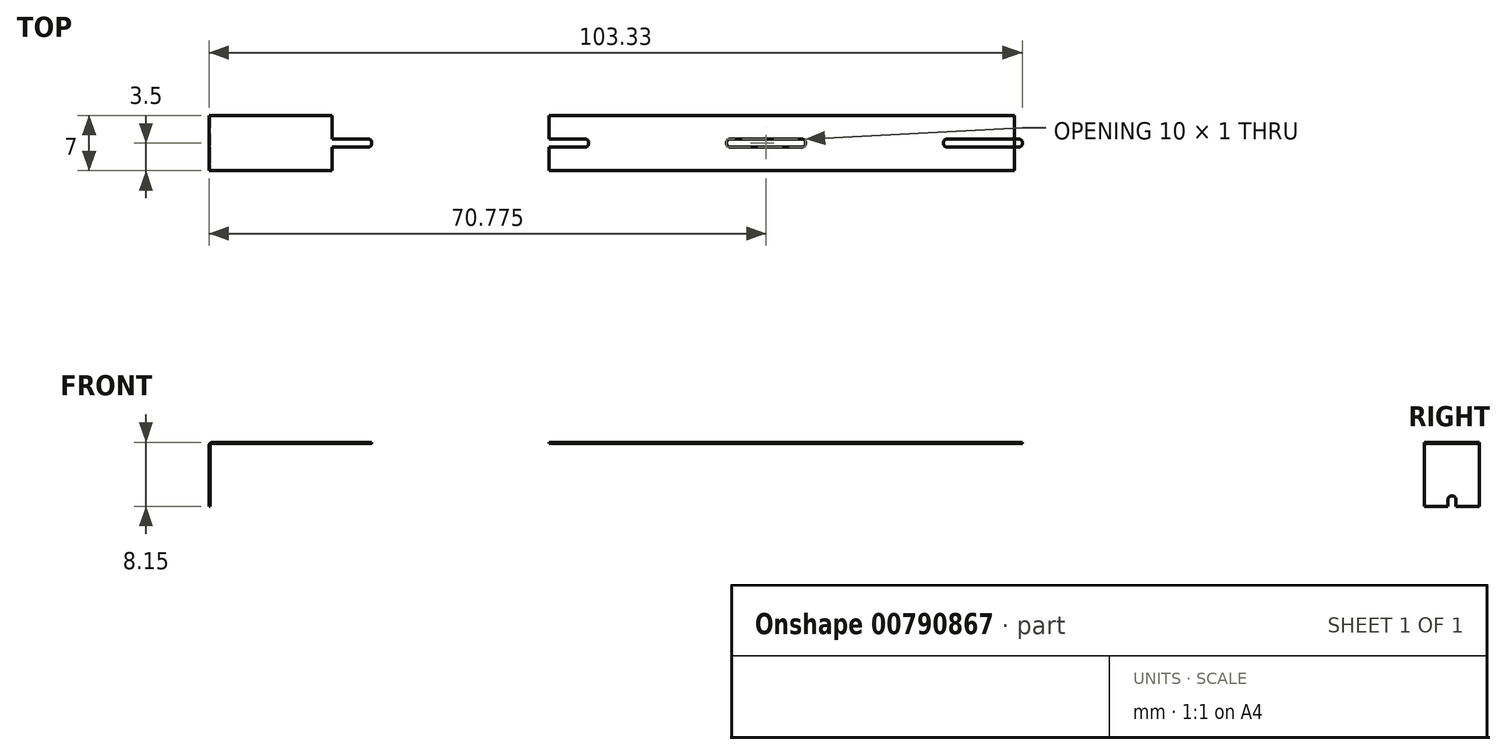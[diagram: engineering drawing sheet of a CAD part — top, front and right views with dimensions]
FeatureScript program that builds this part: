
annotation { "Feature Type Name" : "Feature", "Feature Type Description" : "" }
export const myFeature = defineFeature(function(context is Context, id is Id, definition is map)
    precondition{}
    {
        {
            var Q0;
            Q0=qCreatedBy(makeId("Top.planeOp"),FACE);
            var sketch = newSketch(context, id + "F0", { "sketchPlane" : qUnion([Q0])});
            skPoint(sketch, "E0.middle", {"position": v(0, 0) * mm});
            skLineSegment(sketch, "E1.bottom", {"start": v(-9.18, -0.5) * mm, "end": v(-13.77, -0.5) * mm});
            skLineSegment(sketch, "E1.top", {"start": v(-9.18, 0.5) * mm, "end": v(-13.77, 0.5) * mm});
            skLineSegment(sketch, "E1.left", {"start": v(-8.78, -0.1) * mm, "end": v(-8.78, 0.1) * mm});
            skLineSegment(sketch, "E1.right", {"start": v(-18.78, -0.1) * mm, "end": v(-18.78, 0.1) * mm});
            skPoint(sketch, "E1.middle", {"position": v(-13.78, 0) * mm});
            skPoint(sketch, "E2.visualSharp", {"position": v(-8.78, 0.5) * mm});
            skArc(sketch, "E2.filletArc", {"start": v(-8.78, 0.1) * mm, "mid": v(-8.9, 0.38) * mm, "end": v(-9.18, 0.5) * mm});
            skPoint(sketch, "E3.visualSharp", {"position": v(-8.78, -0.5) * mm});
            skArc(sketch, "E3.filletArc", {"start": v(-9.18, -0.5) * mm, "mid": v(-8.9, -0.38) * mm, "end": v(-8.78, -0.1) * mm});
            skPoint(sketch, "E4.visualSharp", {"position": v(-18.78, 0.5) * mm});
            skArc(sketch, "E4.filletArc", {"start": v(-18.38, 0.5) * mm, "mid": v(-18.66, 0.38) * mm, "end": v(-18.77, 0.1) * mm});
            skPoint(sketch, "E5.visualSharp", {"position": v(-18.78, -0.5) * mm});
            skArc(sketch, "E5.filletArc", {"start": v(-18.77, -0.1) * mm, "mid": v(-18.66, -0.38) * mm, "end": v(-18.38, -0.5) * mm});
            skLineSegment(sketch, "E6", {"start": v(0, 3.5) * mm, "end": v(-13.78, 3.5) * mm});
            skPoint(sketch, "E6.endSnap0", {"position": v(-13.77, 0.5) * mm});
            skLineSegment(sketch, "E7", {"start": v(-13.78, 3.5) * mm, "end": v(-13.78, 0.5) * mm});
            skLineSegment(sketch, "E8.MirrorCS", {"start": v(0, -3.5) * mm, "end": v(-13.78, -3.5) * mm});
            skLineSegment(sketch, "E9.MirrorCS", {"start": v(-13.78, -3.5) * mm, "end": v(-13.78, -0.5) * mm});
            skLineSegment(sketch, "E10.MirrorCS", {"start": v(0, 3.5) * mm, "end": v(13.78, 3.5) * mm});
            skLineSegment(sketch, "E11.MirrorCS", {"start": v(0, -3.5) * mm, "end": v(13.78, -3.5) * mm});
            skLineSegment(sketch, "E12.MirrorCS", {"start": v(8.78, -0.1) * mm, "end": v(8.78, 0.1) * mm});
            skArc(sketch, "E13.MirrorCS", {"start": v(8.78, 0.1) * mm, "mid": v(8.9, 0.38) * mm, "end": v(9.18, 0.5) * mm});
            skArc(sketch, "E14.MirrorCS", {"start": v(18.77, -0.1) * mm, "mid": v(18.66, -0.38) * mm, "end": v(18.38, -0.5) * mm});
            skLineSegment(sketch, "E15.MirrorCS", {"start": v(18.78, -0.1) * mm, "end": v(18.78, 0.1) * mm});
            skArc(sketch, "E16.MirrorCS", {"start": v(18.38, 0.5) * mm, "mid": v(18.66, 0.38) * mm, "end": v(18.77, 0.1) * mm});
            skArc(sketch, "E17.MirrorCS", {"start": v(9.18, -0.5) * mm, "mid": v(8.9, -0.38) * mm, "end": v(8.78, -0.1) * mm});
            skPoint(sketch, "E18.MirrorP", {"position": v(18.78, 0.5) * mm});
            skLineSegment(sketch, "E19.MirrorCS", {"start": v(9.18, 0.5) * mm, "end": v(18.38, 0.5) * mm});
            skLineSegment(sketch, "E20.MirrorCS", {"start": v(9.18, -0.5) * mm, "end": v(18.38, -0.5) * mm});
            skPoint(sketch, "E21.MirrorP", {"position": v(13.77, 0.5) * mm});
            skPoint(sketch, "E22.MirrorP", {"position": v(8.78, 0.5) * mm});
            skPoint(sketch, "E23.MirrorP", {"position": v(18.78, -0.5) * mm});
            skPoint(sketch, "E24.MirrorP", {"position": v(8.78, -0.5) * mm});
            skPoint(sketch, "E25.MirrorP", {"position": v(13.78, 0) * mm});
            skLineSegment(sketch, "E26.MirrorCS", {"start": v(13.78, 3.5) * mm, "end": v(13.78, 0.5) * mm});
            skLineSegment(sketch, "E27.MirrorCS", {"start": v(13.78, -3.5) * mm, "end": v(13.78, -0.5) * mm});
            skPoint(sketch, "E28.1.0.0", {"position": v(36.33, 0.5) * mm});
            skLineSegment(sketch, "E28.1.0.1", {"start": v(27.55, 3.5) * mm, "end": v(41.33, 3.5) * mm});
            skLineSegment(sketch, "E28.1.0.2", {"start": v(36.73, -0.5) * mm, "end": v(45.93, -0.5) * mm});
            skPoint(sketch, "E28.1.0.3", {"position": v(27.55, 0) * mm});
            skLineSegment(sketch, "E28.1.0.4", {"start": v(27.55, -3.5) * mm, "end": v(41.33, -3.5) * mm});
            skPoint(sketch, "E28.1.0.5", {"position": v(41.33, 0.5) * mm});
            skPoint(sketch, "E28.1.0.6", {"position": v(41.33, 0) * mm});
            skPoint(sketch, "E28.1.0.7", {"position": v(46.33, -0.5) * mm});
            skPoint(sketch, "E28.1.0.8", {"position": v(36.33, -0.5) * mm});
            skLineSegment(sketch, "E28.1.0.9", {"start": v(27.55, -3.5) * mm, "end": v(13.78, -3.5) * mm});
            skLineSegment(sketch, "E28.1.0.10", {"start": v(36.73, 0.5) * mm, "end": v(45.93, 0.5) * mm});
            skLineSegment(sketch, "E28.1.0.11", {"start": v(27.55, 3.5) * mm, "end": v(13.78, 3.5) * mm});
            skLineSegment(sketch, "E28.1.0.12", {"start": v(41.33, 3.5) * mm, "end": v(41.33, 0.5) * mm});
            skLineSegment(sketch, "E28.1.0.13", {"start": v(41.33, -3.5) * mm, "end": v(41.33, -0.5) * mm});
            skPoint(sketch, "E28.1.0.14", {"position": v(46.33, 0.5) * mm});
            skArc(sketch, "E28.1.0.15", {"start": v(45.93, 0.5) * mm, "mid": v(46.2, 0.38) * mm, "end": v(46.32, 0.1) * mm});
            skArc(sketch, "E28.1.0.16", {"start": v(36.73, -0.5) * mm, "mid": v(36.44, -0.38) * mm, "end": v(36.33, -0.1) * mm});
            skArc(sketch, "E28.1.0.17", {"start": v(46.33, -0.1) * mm, "mid": v(46.2, -0.38) * mm, "end": v(45.93, -0.5) * mm});
            skArc(sketch, "E28.1.0.18", {"start": v(36.33, 0.1) * mm, "mid": v(36.44, 0.38) * mm, "end": v(36.73, 0.5) * mm});
            skLineSegment(sketch, "E28.1.0.19", {"start": v(36.32, -0.1) * mm, "end": v(36.32, 0.1) * mm});
            skLineSegment(sketch, "E28.1.0.20", {"start": v(46.33, -0.1) * mm, "end": v(46.33, 0.1) * mm});
            skPoint(sketch, "E28.2.0.0", {"position": v(63.88, 0.5) * mm});
            skLineSegment(sketch, "E28.2.0.1", {"start": v(55.1, 3.5) * mm, "end": v(68.88, 3.5) * mm});
            skLineSegment(sketch, "E28.2.0.2", {"start": v(64.28, -0.5) * mm, "end": v(73.48, -0.5) * mm});
            skPoint(sketch, "E28.2.0.3", {"position": v(55.1, 0) * mm});
            skLineSegment(sketch, "E28.2.0.4", {"start": v(55.1, -3.5) * mm, "end": v(68.88, -3.5) * mm});
            skPoint(sketch, "E28.2.0.5", {"position": v(68.88, 0.5) * mm});
            skPoint(sketch, "E28.2.0.6", {"position": v(68.88, 0) * mm});
            skPoint(sketch, "E28.2.0.7", {"position": v(73.88, -0.5) * mm});
            skPoint(sketch, "E28.2.0.8", {"position": v(63.88, -0.5) * mm});
            skLineSegment(sketch, "E28.2.0.9", {"start": v(55.1, -3.5) * mm, "end": v(41.33, -3.5) * mm});
            skLineSegment(sketch, "E28.2.0.10", {"start": v(64.28, 0.5) * mm, "end": v(73.48, 0.5) * mm});
            skLineSegment(sketch, "E28.2.0.11", {"start": v(55.1, 3.5) * mm, "end": v(41.33, 3.5) * mm});
            skLineSegment(sketch, "E28.2.0.12", {"start": v(68.88, 3.5) * mm, "end": v(68.88, 0.5) * mm});
            skLineSegment(sketch, "E28.2.0.13", {"start": v(68.88, -3.5) * mm, "end": v(68.88, -0.5) * mm});
            skPoint(sketch, "E28.2.0.14", {"position": v(73.88, 0.5) * mm});
            skArc(sketch, "E28.2.0.15", {"start": v(73.48, 0.5) * mm, "mid": v(73.76, 0.38) * mm, "end": v(73.88, 0.1) * mm});
            skArc(sketch, "E28.2.0.16", {"start": v(64.28, -0.5) * mm, "mid": v(64, -0.38) * mm, "end": v(63.88, -0.1) * mm});
            skArc(sketch, "E28.2.0.17", {"start": v(73.88, -0.1) * mm, "mid": v(73.76, -0.38) * mm, "end": v(73.48, -0.5) * mm});
            skArc(sketch, "E28.2.0.18", {"start": v(63.88, 0.1) * mm, "mid": v(64, 0.38) * mm, "end": v(64.28, 0.5) * mm});
            skLineSegment(sketch, "E28.2.0.19", {"start": v(63.88, -0.1) * mm, "end": v(63.88, 0.1) * mm});
            skLineSegment(sketch, "E28.2.0.20", {"start": v(73.88, -0.1) * mm, "end": v(73.88, 0.1) * mm});
            skPoint(sketch, "E28.3.0.0", {"position": v(91.43, 0.5) * mm});
            skLineSegment(sketch, "E28.3.0.1", {"start": v(82.65, 3.5) * mm, "end": v(96.43, 3.5) * mm});
            skLineSegment(sketch, "E28.3.0.2", {"start": v(91.83, -0.5) * mm, "end": v(101.03, -0.5) * mm});
            skPoint(sketch, "E28.3.0.3", {"position": v(82.65, 0) * mm});
            skLineSegment(sketch, "E28.3.0.4", {"start": v(82.65, -3.5) * mm, "end": v(96.43, -3.5) * mm});
            skPoint(sketch, "E28.3.0.5", {"position": v(96.43, 0.5) * mm});
            skPoint(sketch, "E28.3.0.6", {"position": v(96.42, 0) * mm});
            skPoint(sketch, "E28.3.0.7", {"position": v(101.42, -0.5) * mm});
            skPoint(sketch, "E28.3.0.8", {"position": v(91.43, -0.5) * mm});
            skLineSegment(sketch, "E28.3.0.9", {"start": v(82.65, -3.5) * mm, "end": v(68.88, -3.5) * mm});
            skLineSegment(sketch, "E28.3.0.10", {"start": v(91.83, 0.5) * mm, "end": v(101.03, 0.5) * mm});
            skLineSegment(sketch, "E28.3.0.11", {"start": v(82.65, 3.5) * mm, "end": v(68.88, 3.5) * mm});
            skLineSegment(sketch, "E28.3.0.12", {"start": v(96.43, 3.5) * mm, "end": v(96.43, 0.5) * mm});
            skLineSegment(sketch, "E28.3.0.13", {"start": v(96.43, -3.5) * mm, "end": v(96.43, -0.5) * mm});
            skPoint(sketch, "E28.3.0.14", {"position": v(101.42, 0.5) * mm});
            skArc(sketch, "E28.3.0.15", {"start": v(101.03, 0.5) * mm, "mid": v(101.3, 0.38) * mm, "end": v(101.42, 0.1) * mm});
            skArc(sketch, "E28.3.0.16", {"start": v(91.83, -0.5) * mm, "mid": v(91.54, -0.38) * mm, "end": v(91.43, -0.1) * mm});
            skArc(sketch, "E28.3.0.17", {"start": v(101.42, -0.1) * mm, "mid": v(101.3, -0.38) * mm, "end": v(101.03, -0.5) * mm});
            skArc(sketch, "E28.3.0.18", {"start": v(91.43, 0.1) * mm, "mid": v(91.54, 0.38) * mm, "end": v(91.83, 0.5) * mm});
            skLineSegment(sketch, "E28.3.0.19", {"start": v(91.43, -0.1) * mm, "end": v(91.43, 0.1) * mm});
            skLineSegment(sketch, "E28.3.0.20", {"start": v(101.42, -0.1) * mm, "end": v(101.42, 0.1) * mm});
            skLineSegment(sketch, "E28.direction1", {"start": v(-13.78, -3.5) * mm, "end": v(13.78, -3.5) * mm, "construction": true});
            skLineSegment(sketch, "E29", {"start": v(0, 3.5) * mm, "end": v(0, -3.5) * mm});
            skLineSegment(sketch, "E30.bottom", {"start": v(96.43, -3.5) * mm, "end": v(100.42, -3.5) * mm});
            skLineSegment(sketch, "E30.top", {"start": v(96.43, 3.5) * mm, "end": v(100.42, 3.5) * mm});
            skLineSegment(sketch, "E30.left", {"start": v(96.43, -3.5) * mm, "end": v(96.43, 3.5) * mm});
            skLineSegment(sketch, "E31", {"start": v(100.42, -3.5) * mm, "end": v(100.42, 3.5) * mm});
            skSolve(sketch);
        }
        {
            var Q0;
            {var subQ8=sQuery(id+"F0.wireOp",EDGE,"E28.3.0.12");Q0=makeQuery(id+"F0.imprint","IMPRINT",FACE,{"disambiguationData":[TD([[makeQuery(id+"F0.imprint","IMPRINT",EDGE,{"derivedFrom":subQ8}),1.0]])]});}
            var Q1;
            {var subQ3=sQuery(id+"F0.wireOp",EDGE,"E14.MirrorCS");Q1=makeQuery(id+"F0.imprint","IMPRINT",FACE,{"disambiguationData":[TD([[makeQuery(id+"F0.imprint","IMPRINT",EDGE,{"derivedFrom":subQ3}),1.0]])]});}
            var Q2;
            {var subQ8=sQuery(id+"F0.wireOp",EDGE,"E28.1.0.12");Q2=makeQuery(id+"F0.imprint","IMPRINT",FACE,{"disambiguationData":[TD([[makeQuery(id+"F0.imprint","IMPRINT",EDGE,{"derivedFrom":subQ8}),1.0]])]});}
            var Q3;
            {var subQ8=sQuery(id+"F0.wireOp",EDGE,"E28.2.0.12");Q3=makeQuery(id+"F0.imprint","IMPRINT",FACE,{"disambiguationData":[TD([[makeQuery(id+"F0.imprint","IMPRINT",EDGE,{"derivedFrom":subQ8}),1.0]])]});}
            var Q4;
            Q4=makeQuery(id+"F0.imprint","IMPRINT",FACE,{"disambiguationData":[TD([[makeQuery(id+"F0.imprint","IMPRINT",EDGE,{"derivedFrom":sQuery(id+"F0.wireOp",EDGE,"E10.MirrorCS")}),-1.0]])]});
            var Q5;
            {var subQ5=sQuery(id+"F0.wireOp",EDGE,"E30.top");Q5=makeQuery(id+"F0.imprint","IMPRINT",FACE,{"disambiguationData":[TD([[makeQuery(id+"F0.imprint","IMPRINT",EDGE,{"derivedFrom":subQ5}),-1.0]])]});}
            var Q6;
            {var subQ5=sQuery(id+"F0.wireOp",EDGE,"E30.bottom");Q6=makeQuery(id+"F0.imprint","IMPRINT",FACE,{"disambiguationData":[TD([[makeQuery(id+"F0.imprint","IMPRINT",EDGE,{"derivedFrom":subQ5}),1.0]])]});}
            var Q7;
            {var subQ11=sQuery(id+"F0.wireOp",EDGE,"E28.3.0.15");Q7=makeQuery(id+"F0.imprint","IMPRINT",FACE,{"disambiguationData":[TD([[makeQuery(id+"F0.imprint","IMPRINT",EDGE,{"derivedFrom":subQ11}),1.0]])]});}
            extrude(context, id + "F1", {"entities" : qUnion([Q0, Q1, Q2, Q3, Q4, Q5, Q6, Q7]), "depth" : 0.15 * mm, "offsetDistance" : 25 * mm});
        }
        {
            var Q0;
            Q0=makeQuery(id+"F1.opExtrude","SWEPT_FACE",FACE,{"disambiguationData":[OSD([sQuery(id+"F0.wireOp",EDGE,"E29")])]});
            extrude(context, id + "F2", {"entities" : qUnion([Q0]), "operationType" : NewBodyOperationType.ADD, "depth" : 1.9 * mm, "offsetDistance" : 25 * mm});
        }
        {
            var Q0;
            {var subQ0=sQuery(id+"F0.wireOp",EDGE,"E29");Q0=makeQuery(id+"F2.boolean.opBoolean","MERGE",FACE,{"derivedFrom":[makeQuery(id+"F1.opExtrude","CAP_FACE",FACE,{"disambiguationData":[OSD([sQuery(id+"F0.wireOp",EDGE,"E10.MirrorCS"),sQuery(id+"F0.wireOp",EDGE,"E11.MirrorCS"),sQuery(id+"F0.wireOp",EDGE,"E12.MirrorCS"),sQuery(id+"F0.wireOp",EDGE,"E13.MirrorCS"),sQuery(id+"F0.wireOp",EDGE,"E14.MirrorCS"),sQuery(id+"F0.wireOp",EDGE,"E15.MirrorCS"),sQuery(id+"F0.wireOp",EDGE,"E16.MirrorCS"),sQuery(id+"F0.wireOp",EDGE,"E17.MirrorCS"),sQuery(id+"F0.wireOp",EDGE,"E19.MirrorCS"),sQuery(id+"F0.wireOp",EDGE,"E20.MirrorCS"),sQuery(id+"F0.wireOp",EDGE,"E28.1.0.1"),sQuery(id+"F0.wireOp",EDGE,"E28.1.0.2"),sQuery(id+"F0.wireOp",EDGE,"E28.1.0.4"),sQuery(id+"F0.wireOp",EDGE,"E28.1.0.9"),sQuery(id+"F0.wireOp",EDGE,"E28.1.0.10"),sQuery(id+"F0.wireOp",EDGE,"E28.1.0.11"),sQuery(id+"F0.wireOp",EDGE,"E28.1.0.15"),sQuery(id+"F0.wireOp",EDGE,"E28.1.0.16"),sQuery(id+"F0.wireOp",EDGE,"E28.1.0.17"),sQuery(id+"F0.wireOp",EDGE,"E28.1.0.18"),sQuery(id+"F0.wireOp",EDGE,"E28.1.0.19"),sQuery(id+"F0.wireOp",EDGE,"E28.1.0.20"),sQuery(id+"F0.wireOp",EDGE,"E28.2.0.1"),sQuery(id+"F0.wireOp",EDGE,"E28.2.0.2"),sQuery(id+"F0.wireOp",EDGE,"E28.2.0.4"),sQuery(id+"F0.wireOp",EDGE,"E28.2.0.9"),sQuery(id+"F0.wireOp",EDGE,"E28.2.0.10"),sQuery(id+"F0.wireOp",EDGE,"E28.2.0.11"),sQuery(id+"F0.wireOp",EDGE,"E28.2.0.15"),sQuery(id+"F0.wireOp",EDGE,"E28.2.0.16"),sQuery(id+"F0.wireOp",EDGE,"E28.2.0.17"),sQuery(id+"F0.wireOp",EDGE,"E28.2.0.18"),sQuery(id+"F0.wireOp",EDGE,"E28.2.0.19"),sQuery(id+"F0.wireOp",EDGE,"E28.2.0.20"),sQuery(id+"F0.wireOp",EDGE,"E28.3.0.1"),sQuery(id+"F0.wireOp",EDGE,"E28.3.0.2"),sQuery(id+"F0.wireOp",EDGE,"E28.3.0.4"),sQuery(id+"F0.wireOp",EDGE,"E28.3.0.9"),sQuery(id+"F0.wireOp",EDGE,"E28.3.0.10"),sQuery(id+"F0.wireOp",EDGE,"E28.3.0.11"),sQuery(id+"F0.wireOp",EDGE,"E28.3.0.12"),sQuery(id+"F0.wireOp",EDGE,"E28.3.0.13"),sQuery(id+"F0.wireOp",EDGE,"E28.3.0.16"),sQuery(id+"F0.wireOp",EDGE,"E28.3.0.18"),sQuery(id+"F0.wireOp",EDGE,"E28.3.0.19"),subQ0])],"isStart":true}),makeQuery(id+"F2.opExtrude","SWEPT_FACE",FACE,{"disambiguationData":[OSD([subQ0]),TDD([makeQuery(id+"F1.opExtrude","CAP_EDGE",EDGE,{"disambiguationData":[OSD([subQ0])],"isStart":true})])]})]});}
            var sketch = newSketch(context, id + "F3", { "sketchPlane" : qUnion([Q0])});
            skLineSegment(sketch, "E32.bottom", {"start": v(-1.9, -3.5) * mm, "end": v(-1.75, -3.5) * mm});
            skLineSegment(sketch, "E32.top", {"start": v(-1.9, 3.5) * mm, "end": v(-1.75, 3.5) * mm});
            skLineSegment(sketch, "E32.left", {"start": v(-1.9, -3.5) * mm, "end": v(-1.9, 3.5) * mm});
            skLineSegment(sketch, "E32.right", {"start": v(-1.75, -3.5) * mm, "end": v(-1.75, 3.5) * mm});
            skSolve(sketch);
        }
        {
            var Q0;
            Q0=qSketchRegion(id+"F3",true);
            extrude(context, id + "F4", {"entities" : qUnion([Q0]), "operationType" : NewBodyOperationType.ADD, "depth" : 8 * mm, "offsetDistance" : 25 * mm});
        }
        {
            var Q0;
            Q0=makeQuery(id+"F4.boolean.opBoolean","MERGE",FACE,{"derivedFrom":[makeQuery(id+"F2.opExtrude","CAP_FACE",FACE,{"disambiguationData":[OSD([sQuery(id+"F0.wireOp",EDGE,"E29")])],"isStart":false}),makeQuery(id+"F4.opExtrude","SWEPT_FACE",FACE,{"disambiguationData":[OSD([sQuery(id+"F3.wireOp",EDGE,"E32.left")])]})]});
            var sketch = newSketch(context, id + "F5", { "sketchPlane" : qUnion([Q0])});
            skLineSegment(sketch, "E33.bottom", {"start": v(0.1, -6.7) * mm, "end": v(-0.1, -6.7) * mm});
            skLineSegment(sketch, "E33.top", {"start": v(0.5, -16.7) * mm, "end": v(-0.5, -16.7) * mm});
            skLineSegment(sketch, "E33.left", {"start": v(0.5, -7.1) * mm, "end": v(0.5, -16.7) * mm});
            skLineSegment(sketch, "E33.right", {"start": v(-0.5, -7.1) * mm, "end": v(-0.5, -16.7) * mm});
            skPoint(sketch, "E33.middle", {"position": v(0, -11.7) * mm});
            skPoint(sketch, "E33.middle.positionSnap0", {"position": v(0, -8) * mm});
            skPoint(sketch, "E33.centerSnap0", {"position": v(0, -8) * mm});
            skPoint(sketch, "E34.visualSharp", {"position": v(-0.5, -6.7) * mm});
            skArc(sketch, "E34.filletArc", {"start": v(-0.1, -6.7) * mm, "mid": v(-0.38, -6.82) * mm, "end": v(-0.5, -7.1) * mm});
            skPoint(sketch, "E35.visualSharp", {"position": v(0.5, -6.7) * mm});
            skArc(sketch, "E35.filletArc", {"start": v(0.5, -7.1) * mm, "mid": v(0.38, -6.82) * mm, "end": v(0.1, -6.7) * mm});
            skSolve(sketch);
        }
        {
            var Q0;
            Q0=makeQuery(id+"F5.imprint","IMPRINT",FACE,{"disambiguationData":[TD([[makeQuery(id+"F5.imprint","IMPRINT",EDGE,{"derivedFrom":sQuery(id+"F5.wireOp",EDGE,"E33.bottom")}),1.0]])]});
            extrude(context, id + "F6", {"entities" : qUnion([Q0]), "operationType" : NewBodyOperationType.REMOVE, "oppositeDirection" : true, "depth" : 25 * mm, "offsetDistance" : 25 * mm});
        }
        {
            var Q0;
            {var subQ0=sQuery(id+"F0.wireOp",EDGE,"E29");Q0=makeQuery(id+"F2.opExtrude","CAP_EDGE",EDGE,{"disambiguationData":[OSD([subQ0]),TDD([makeQuery(id+"F1.opExtrude","CAP_EDGE",EDGE,{"disambiguationData":[OSD([subQ0])],"isStart":false})])],"isStart":false});}
            var Q1;
            Q1=makeQuery(id+"F4.opExtrude","CAP_EDGE",EDGE,{"disambiguationData":[OSD([sQuery(id+"F3.wireOp",EDGE,"E32.right")])],"isStart":true});
            fillet(context, id + "F7", {"entities" : qUnion([Q0, Q1]), "radius" : 0.5 * mm, "tangentPropagation" : true, "allowEdgeOverflow" : false});
        }
    });
